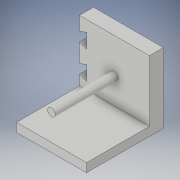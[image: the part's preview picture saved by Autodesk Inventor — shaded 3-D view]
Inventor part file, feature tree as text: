
AUTODESK INVENTOR PART (.ipt)
format: ipt  version: 2019 (Build 230136000, 136)  size: 128,000 bytes
history: native  units: in
note: dims shown in document units (in); Inventor stores cm internally (conversion verified against a paired STEP export)
features: extrude x2, sketch x2
ambient origin geometry x8: Origin, YZ Plane, XZ Plane, XY Plane, X Axis, Y Axis, Z Axis, Center Point
bodies: Solid1 (feature_tree)
feature tree (4):
  extrude  "Extrusion1"  Depth=1.9685in
  extrude  "Extrusion2"  Depth=1.7717in
  sketch  "Sketch1"  dims[d0=1.9685in d1=1.9685in]
  sketch  "Sketch2"  dims[d2=1.9685in d5=0.481in d6=0.481in d7=0.1969in d8=0.4094in d9=0.481in d10=0.481in d11=0.7953in d12=0.2047in d13=0.2047in d14=0.4094in d15=1.5827in d16=0.481in d17=0.481in d18=0.2604in d19=0.2604in d21=0.3937in d22=0.0in d23=0.2205in d24=1.7717in d25=0.0in]
